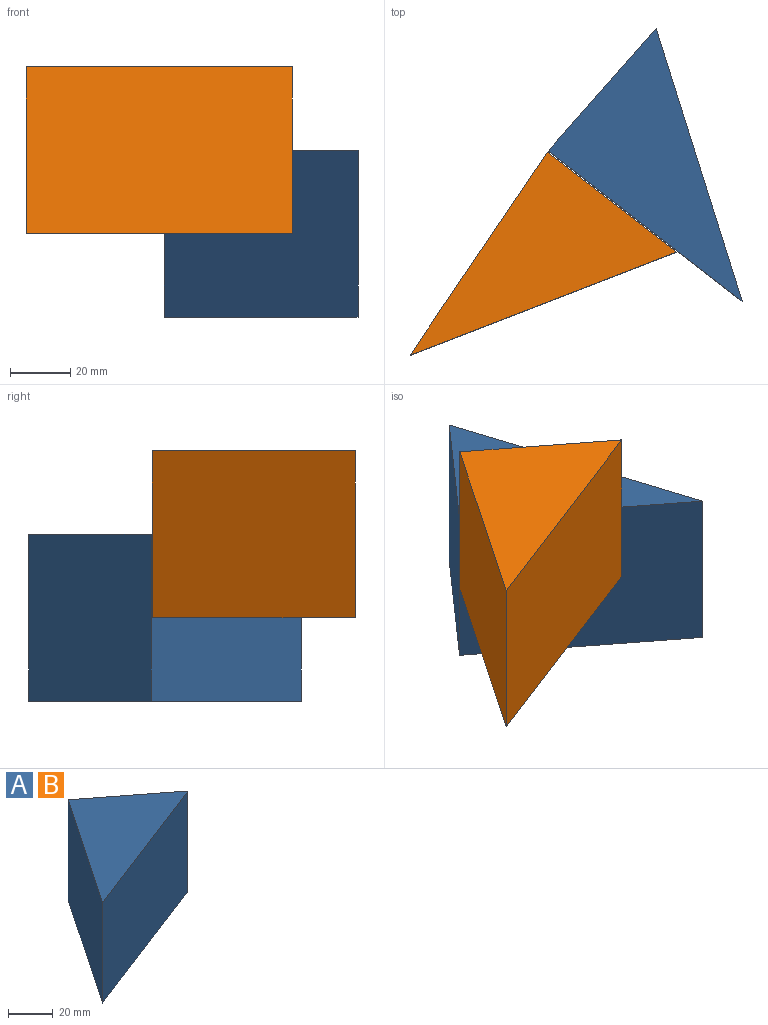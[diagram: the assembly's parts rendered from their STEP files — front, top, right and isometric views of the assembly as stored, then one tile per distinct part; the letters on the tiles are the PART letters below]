
ASSEMBLY  parts=2 mates=1
PART A: 5 faces, bbox 88.4x67.3x55.4 mm
  f0: plane 67.35x55.37mm, normal (-0.83,0.56,0), area 4501.4mm2, adj f1,f2,f3,f4
  f1: plane 88.36x55.37mm, normal (0.36,-0.93,0), area 5246.7mm2, adj f0,f2,f3,f4
  f2: plane 55.37x42.83mm, normal (0.61,0.79,0), area 2998.6mm2, adj f0,f1,f3,f4
  f3: plane 88.36x67.35mm, normal (0,0,1), area 2196.7mm2, adj f0,f1,f2
  f4: plane 88.36x67.35mm, normal (0,0,-1), area 2196.7mm2, adj f0,f1,f2
PART B: same geometry as A
PLACE A rot(axis=(0,0,1),86.3deg) t=(58.84,39.87,-12.31)mm
PLACE B t=(10.43,11.78,15.37)mm fixed
MATE slider B.f2 <-> A.f0  axis (0.61,0.79,0) through (19.72,51.25,43.06)mm
